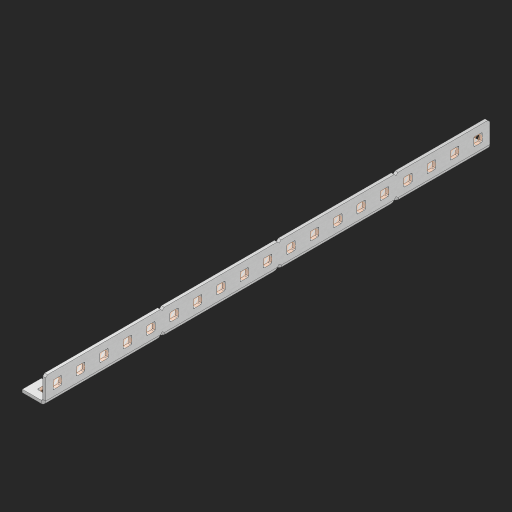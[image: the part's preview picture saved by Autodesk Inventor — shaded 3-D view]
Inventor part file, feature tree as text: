
AUTODESK INVENTOR PART (.ipt)
format: ipt  version: 2023 (Build 270158000, 158)  size: 952,320 bytes
history: native  units: in
note: dims shown in document units (in); Inventor stores cm internally (conversion verified against a paired STEP export)
features: other x205, extrude x55, sheet_metal_op x11, sketch x10, pattern_linear x2, mirror x1, chamfer x1
ambient origin geometry x8: Origin, YZ Plane, XZ Plane, XY Plane, X Axis, Y Axis, Z Axis, Center Point
bodies: Solid1 (feature_tree), Body (feature_tree)
feature tree (285):
  other  "Alu Half C 1x2x1x19"
  other  "Table"
  other  "Alu C 1x2x1x35"
  other  "Alu C 1x2x1x34"
  other  "Alu C 1x2x1x33"
  other  "Alu C 1x2x1x32"
  other  "Alu C 1x2x1x31"
  other  "Alu C 1x2x1x30"
  other  "Alu C 1x2x1x29"
  other  "Alu C 1x2x1x28"
  other  "Alu C 1x2x1x27"
  other  "Alu C 1x2x1x26"
  other  "Alu C 1x2x1x25"
  other  "Alu C 1x2x1x24"
  other  "Alu C 1x2x1x23"
  other  "Alu C 1x2x1x22"
  other  "Alu C 1x2x1x21"
  other  "Alu C 1x2x1x20"
  other  "Alu C 1x2x1x19"
  other  "Alu C 1x2x1x18"
  other  "Alu C 1x2x1x17"
  other  "Alu C 1x2x1x16"
  other  "Alu C 1x2x1x15"
  other  "Alu C 1x2x1x14"
  other  "Alu C 1x2x1x13"
  other  "Alu C 1x2x1x12"
  other  "Alu C 1x2x1x11"
  other  "Alu C 1x2x1x10"
  other  "Alu C 1x2x1x9"
  other  "Alu C 1x2x1x8"
  other  "Alu C 1x2x1x7"
  other  "Alu C 1x2x1x6"
  other  "Alu C 1x2x1x5"
  other  "Alu C 1x2x1x4"
  other  "Alu C 1x2x1x3"
  other  "Alu C 1x2x1x2"
  other  "Alu C 1x2x1x1"
  other  "Steel C 1x2x1x35"
  other  "Steel C 1x2x1x34"
  other  "Steel C 1x2x1x33"
  other  "Steel C 1x2x1x32"
  other  "Steel C 1x2x1x31"
  other  "Steel C 1x2x1x30"
  other  "Steel C 1x2x1x29"
  other  "Steel C 1x2x1x28"
  other  "Steel C 1x2x1x27"
  other  "Steel C 1x2x1x26"
  other  "Steel C 1x2x1x25"
  other  "Steel C 1x2x1x24"
  other  "Steel C 1x2x1x23"
  other  "Steel C 1x2x1x22"
  other  "Steel C 1x2x1x21"
  other  "Steel C 1x2x1x20"
  other  "Steel C 1x2x1x19"
  other  "Steel C 1x2x1x18"
  other  "Steel C 1x2x1x17"
  other  "Steel C 1x2x1x16"
  other  "Steel C 1x2x1x15"
  other  "Steel C 1x2x1x14"
  other  "Steel C 1x2x1x13"
  other  "Steel C 1x2x1x12"
  other  "Steel C 1x2x1x11"
  other  "Steel C 1x2x1x10"
  other  "Steel C 1x2x1x9"
  other  "Steel C 1x2x1x8"
  other  "Steel C 1x2x1x7"
  other  "Steel C 1x2x1x6"
  other  "Steel C 1x2x1x5"
  other  "Steel C 1x2x1x4"
  other  "Steel C 1x2x1x3"
  other  "Steel C 1x2x1x2"
  other  "Steel C 1x2x1x1"
  other  "Alu Half C 1x2x1x35"
  other  "Alu Half C 1x2x1x34"
  other  "Alu Half C 1x2x1x33"
  other  "Alu Half C 1x2x1x32"
  other  "Alu Half C 1x2x1x31"
  other  "Alu Half C 1x2x1x30"
  other  "Alu Half C 1x2x1x29"
  other  "Alu Half C 1x2x1x28"
  other  "Alu Half C 1x2x1x27"
  other  "Alu Half C 1x2x1x26"
  other  "Alu Half C 1x2x1x25"
  other  "Alu Half C 1x2x1x24"
  other  "Alu Half C 1x2x1x23"
  other  "Alu Half C 1x2x1x22"
  other  "Alu Half C 1x2x1x21"
  other  "Alu Half C 1x2x1x20"
  other  "Alu Half C 1x2x1x18"
  other  "Alu Half C 1x2x1x17"
  other  "Alu Half C 1x2x1x16"
  other  "Alu Half C 1x2x1x15"
  other  "Alu Half C 1x2x1x14"
  other  "Alu Half C 1x2x1x13"
  other  "Alu Half C 1x2x1x12"
  other  "Alu Half C 1x2x1x11"
  other  "Alu Half C 1x2x1x10"
  other  "Alu Half C 1x2x1x9"
  other  "Alu Half C 1x2x1x8"
  other  "Alu Half C 1x2x1x7"
  other  "Alu Half C 1x2x1x6"
  other  "Alu Half C 1x2x1x5"
  other  "Alu Half C 1x2x1x4"
  other  "Alu Half C 1x2x1x3"
  other  "Alu Half C 1x2x1x2"
  other  "Alu Half C 1x2x1x1"
  other  "Steel Half C 1x2x1x35"
  other  "Steel Half C 1x2x1x34"
  other  "Steel Half C 1x2x1x33"
  other  "Steel Half C 1x2x1x32"
  other  "Steel Half C 1x2x1x31"
  other  "Steel Half C 1x2x1x30"
  other  "Steel Half C 1x2x1x29"
  other  "Steel Half C 1x2x1x28"
  other  "Steel Half C 1x2x1x27"
  other  "Steel Half C 1x2x1x26"
  other  "Steel Half C 1x2x1x25"
  other  "Steel Half C 1x2x1x24"
  other  "Steel Half C 1x2x1x23"
  other  "Steel Half C 1x2x1x22"
  other  "Steel Half C 1x2x1x21"
  other  "Steel Half C 1x2x1x20"
  other  "Steel Half C 1x2x1x19"
  other  "Steel Half C 1x2x1x18"
  other  "Steel Half C 1x2x1x17"
  other  "Steel Half C 1x2x1x16"
  other  "Steel Half C 1x2x1x15"
  other  "Steel Half C 1x2x1x14"
  other  "Steel Half C 1x2x1x13"
  other  "Steel Half C 1x2x1x12"
  other  "Steel Half C 1x2x1x11"
  other  "Steel Half C 1x2x1x10"
  other  "Steel Half C 1x2x1x9"
  other  "Steel Half C 1x2x1x8"
  other  "Steel Half C 1x2x1x7"
  other  "Steel Half C 1x2x1x6"
  other  "Steel Half C 1x2x1x5"
  other  "Steel Half C 1x2x1x4"
  other  "Steel Half C 1x2x1x3"
  other  "Steel Half C 1x2x1x2"
  other  "Steel Half C 1x2x1x1"
  sheet_metal_op  "Flanges"
  other  "Flange Pattern Plane"
  other  "Flange Pattern Sketch"
  sheet_metal_op  "Flange Pattern"
  sheet_metal_op  "Body Pattern"
  pattern_linear  "Center Pattern"  Spacing1=0.0625in  [1 undecoded]
  other  "Arc Length"
  mirror  "Notch Mirror"
  pattern_linear  "Notch Pattern"  Spacing1=0.182in  [1 undecoded]
  chamfer  "End Chamfer"
  extrude  "Half Cut"  Depth=0.02in
  sketch  "Sketch1"  dims[d0=1.0in]
  other  "Plate1"
  sketch  "Sketch2"  dims[d1=9.5in]
  other  "Plate2"
  sheet_metal_op  "Bend1"
  sheet_metal_op  "Corner1"
  sketch  "Sketch3"  dims[d2=0.0625in]
  sketch  "Sketch7"  dims[d3=0.0625in]
  other  "Srf1"
  other  "Srf2"
  sketch  "Sketch8"  dims[d4=0.0312in]
  sketch  "Sketch9"  dims[d5=0.125in]
  other  "Srf91"
  sheet_metal_op  "Body Pattern Sketch"
  other  "Srf92"
  sketch  "Sketch13"  dims[d6=0.0625in]
  sketch  "Sketch14"  dims[d7=0.5in d8=90.0deg d9=0.0312in]
  sketch  "Sketch15"  dims[d10=0.25in]
  sketch  "Sketch16"  dims[d11=0.0625in d12=0.0625in d16=0.182in d17=0.02in d18=0.0625in d19=0.0in d20=0.25in d21=0.25in d38=7.4803in d40=0.5in d41=0.3937in d43=1.0in d46=0.172in d47=1.0in d48=0.0in d49=0.182in d50=0.02in d51=0.25in d52=0.25in d53=0.0625in d54=0.0in d55=0.172in d56=1.0in d57=0.0in d58=0.25in d60=7.4803in d62=0.5in d63=0.3937in d65=0.5in d85=0.1473in d86=0.1782in d88=0.04in d89=0.0625in d90=0.0in d91=0.04in d92=0.0491in d95=2.5in d96=0.04in d97=0.25in d98=45.0deg d99=0.25in d100=0.5in d101=0.0in d102=2.497in d106=0.182in d107=0.02in d108=0.5in d109=0.5in d110=0.0625in d111=0.0in d112=0.172in d113=0.5in d114=0.0in d117=0.5in d118=0.5in d119=0.5in]
  other  "Srf786"
  other  "Srf823"
  other  "Srf824"
  other  "Srf825"
  other  "Srf826"
  other  "Srf827"
  other  "Srf828"
  other  "Srf829"
  other  "Srf856"
  other  "Srf857"
  other  "Srf858"
  other  "Srf859"
  other  "Srf860"
  other  "Srf861"
  other  "Srf862"
  other  "Srf889"
  other  "Srf890"
  other  "Srf891"
  other  "Srf892"
  other  "Srf893"
  other  "Srf894"
  other  "Srf895"
  other  "Srf896"
  other  "Srf922"
  other  "Srf923"
  other  "Srf924"
  other  "Srf925"
  other  "Srf926"
  other  "Srf959"
  other  "Srf960"
  other  "Srf961"
  other  "Srf962"
  other  "Srf963"
  other  "Srf996"
  other  "Srf997"
  other  "Srf998"
  other  "Srf999"
  other  "Srf1000"
  other  "Srf1143"
  other  "Srf1144"
  other  "Srf1145"
  other  "Srf1146"
  other  "Srf1147"
  other  "Srf1199"
  other  "Srf1200"
  other  "Srf1201"
  other  "Srf1202"
  other  "Srf1203"
  other  "Srf1255"
  other  "Srf1256"
  other  "Srf1257"
  other  "Srf1258"
  other  "Srf1259"
  sheet_metal_op  "Flange Stamp"
  sheet_metal_op  "Flange Circle"
  sheet_metal_op  "Body Stamp"
  sheet_metal_op  "Body Circle"
  other  "Center Stamp"
  other  "Center Circle"
  sheet_metal_op  "Notch"
  extrude  "ExtrusionSrf2"  Depth=0.0625in
  extrude  "ExtrusionSrf92"  TaperAngle=0.0deg  [1 undecoded]
  extrude  "ExtrusionSrf823"  Depth=0.5in
  extrude  "ExtrusionSrf824"  Depth=0.5in
  extrude  "ExtrusionSrf825"  Depth=0.5in
  extrude  "ExtrusionSrf826"  Depth=0.5in
  extrude  "ExtrusionSrf827"  Depth=1.0in TaperAngle=0.0deg
  extrude  "ExtrusionSrf828"  Depth=0.182in
  extrude  "ExtrusionSrf829"  Depth=0.02in
  extrude  "ExtrusionSrf856"  Depth=0.5in
  extrude  "ExtrusionSrf857"  Depth=0.5in
  extrude  "ExtrusionSrf858"  Depth=0.0625in
  extrude  "ExtrusionSrf859"  TaperAngle=0.0deg  [1 undecoded]
  extrude  "ExtrusionSrf860"  Depth=0.5in
  extrude  "ExtrusionSrf861"  Depth=1.0in TaperAngle=0.0deg
  extrude  "ExtrusionSrf862"  Depth=0.5in
  extrude  "ExtrusionSrf889"  Depth=0.5in
  extrude  "ExtrusionSrf890"  Depth=0.5in
  extrude  "ExtrusionSrf891"  Depth=0.5in
  extrude  "ExtrusionSrf892"  Depth=0.5in
  extrude  "ExtrusionSrf893"  Depth=0.5in
  extrude  "ExtrusionSrf894"  Depth=0.0625in
  extrude  "ExtrusionSrf895"  TaperAngle=0.0deg  [1 undecoded]
  extrude  "ExtrusionSrf896"  Depth=0.5in
  extrude  "ExtrusionSrf922"  Depth=0.5in
  extrude  "ExtrusionSrf923"  Depth=0.5in
  extrude  "ExtrusionSrf924"  Depth=0.5in TaperAngle=45.0deg
  extrude  "ExtrusionSrf925"  Depth=0.5in
  extrude  "ExtrusionSrf926"  Depth=0.5in TaperAngle=0.0deg
  extrude  "ExtrusionSrf959"  Depth=0.5in
  extrude  "ExtrusionSrf960"  Depth=0.182in
  extrude  "ExtrusionSrf961"  Depth=0.02in
  extrude  "ExtrusionSrf962"  Depth=0.5in
  extrude  "ExtrusionSrf963"  Depth=0.5in
  extrude  "ExtrusionSrf996"  Depth=0.0625in
  extrude  "ExtrusionSrf997"  TaperAngle=0.0deg  [1 undecoded]
  extrude  "ExtrusionSrf998"  Depth=0.5in
  extrude  "ExtrusionSrf999"  Depth=0.5in TaperAngle=0.0deg
  extrude  "ExtrusionSrf1000"  Depth=0.5in
  extrude  "ExtrusionSrf1143"  Depth=0.5in
  extrude  "ExtrusionSrf1144"  Depth=0.5in
  extrude  "ExtrusionSrf1145"  [1 undecoded]
  extrude  "ExtrusionSrf1146"  [1 undecoded]
  extrude  "ExtrusionSrf1147"  [1 undecoded]
  extrude  "ExtrusionSrf1199"  [1 undecoded]
  extrude  "ExtrusionSrf1200"  [1 undecoded]
  extrude  "ExtrusionSrf1201"  [1 undecoded]
  extrude  "ExtrusionSrf1202"  [1 undecoded]
  extrude  "ExtrusionSrf1203"  [1 undecoded]
  extrude  "ExtrusionSrf1255"  [1 undecoded]
  extrude  "ExtrusionSrf1256"  [1 undecoded]
  extrude  "ExtrusionSrf1257"  [1 undecoded]
  extrude  "ExtrusionSrf1258"  [1 undecoded]
  extrude  "ExtrusionSrf1259"  [1 undecoded]
note: 19 required parameter values undecoded (feature->parameter linkage not recoverable at this tier; creation-order binding heuristic only, values carry confidence <= 0.55)
